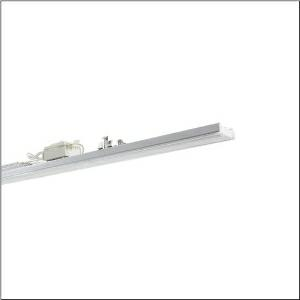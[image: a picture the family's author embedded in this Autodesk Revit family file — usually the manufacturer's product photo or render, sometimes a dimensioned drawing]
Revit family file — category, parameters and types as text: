
# Revit family: licross_r__21_recessed_ho_52te12dv4l2m_40f6
name_source: partatom
category: Lighting Fixtures
units: mm (PartAtom-declared; Revit-internal decimal feet)

## family parameters
Cut with Voids When Loaded = No
Host = Face
Light Source = No
Part Type = Normal
Room Calculation Point = No
Round Connector Dimension = Use Diameter
Shared = No

## types (1)
- --- (1 x LED, 22710 lm, 125.6 W, 4000K)
    Apparent Load = 126 VA
    CIE Flux Codes = 69 91 98 100 100
    Color Rendering = 80
    Color Temperature = 4000K
    Default Elevation = 1800 mm
    Description = Licross® 21 Recessed HO, luminaire insert, of sheet steel, galvanised, coil coated, white, length: 2.250mm, width: 66mm, height: 67mm, LED rated luminous flux: 22.710lm, light colour: 840, control gear: DALI 2, with plug, 5-pole, with phase selection, mains connection: 220..240V, AC, 50/60Hz, rated input power: 126W, internal wiring halogen-free, primary optical cover: cover, of PMMA, light emission: direct distribution, primary light characteristic: symmetric, protection rating (complete): IP54, insulation class (complete): insulation class I (protective earthing), certification: CE, ENEC, VDE, UKCA, protection symbol: D if used in an environment with non-conductive dust loads with corresponding accessories, impact resistance: IK06, permissible ambient temperature for indoor applications: -40..+30°C, corresponds to IFS (International Featured Standards) requirements for safety and quality in the food industry, reducing of maximum allowable ambient temperature of 5°C with ceiling mounting, LABS conformity tested according to VDMA 24364:2018-05, packaging unit: 1 piece
    Height = 58 mm
    Lamp = 1 x LED
    Lamp Light Flux = 22710 lm
    Lamp Power = 125.6 W
    Lamp count = 1
    Length = 2250 mm
    Luminous efficacy = 181 lm/W
    Manufacturer = Siteco
    ModVariant = No
    Model = 52TE12DV4L2M
    Mounting Place = Ceiling
    Mounting Type = Pendant
    Number of Poles = 1
    OnlyDefault = Yes
    Power Factor = 1
    Product Name = Licross® 21 Recessed HO
    Product group = luminaire insert | ceiling pendant
    ProductGroupID = 902
    Protection Class = Protection class I
    Protection Degree = IP 54
    RLX_Detail_Level = 1
    RLX_Emergency_Light_Flux = 0 lm
    RLX_Emergency_Type = 0
    RLX_Emergency_Type_DB = No
    RlxData = <blob elided: 29769 chars, md5=7ce42dbd>
    Socket = socket
    Standby Power = 0 W
    System Light Flux = 22710 lm
    System Power = 126 W
    Type Comments = factory setting: luminous flux: 100 % | dim-lin: 254 | 489 mA
    Type Image = l_1296930.jpg
    URL = http://relux.com
    VarID = @adj_138163
    Voltage = 0 V
    Weight = 0.00 kg
    Width = 66 mm

## geometry (parser evidence)
native form markers: Blend x4, Sweep x9
no freeform markers — native parametric forms only
